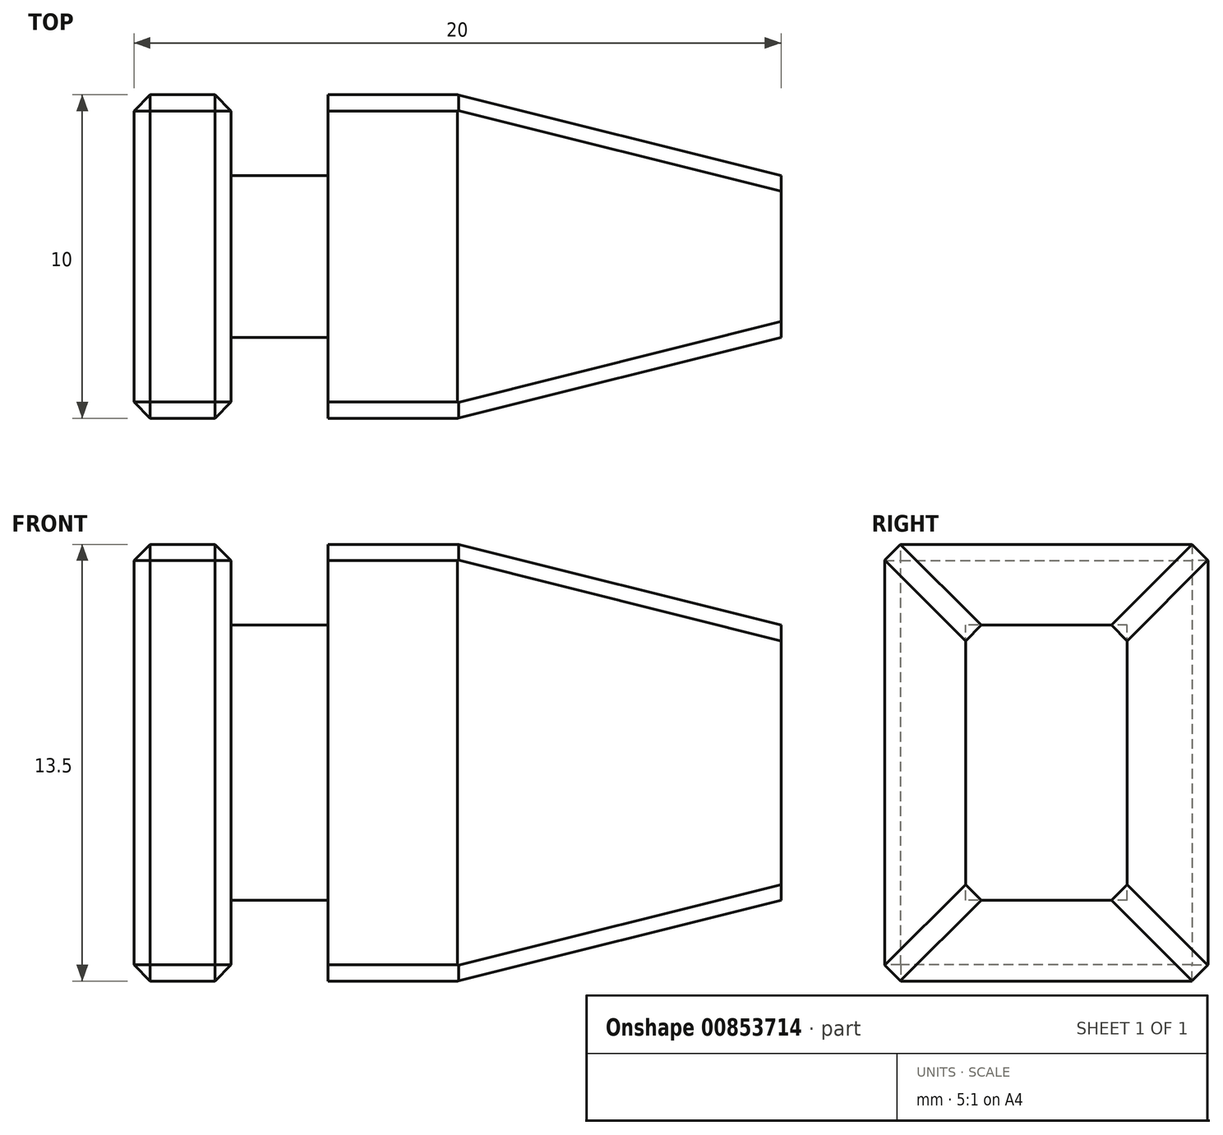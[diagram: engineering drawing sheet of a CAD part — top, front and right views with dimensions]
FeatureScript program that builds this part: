
annotation { "Feature Type Name" : "Feature", "Feature Type Description" : "" }
export const myFeature = defineFeature(function(context is Context, id is Id, definition is map)
    precondition{}
    {
        {
            var Q0;
            Q0=qCreatedBy(makeId("Front.planeOp"),FACE);
            var sketch = newSketch(context, id + "F0", { "sketchPlane" : qUnion([Q0])});
            skLineSegment(sketch, "E0.bottom", {"start": v(0, 0) * mm, "end": v(20, 0) * mm});
            skLineSegment(sketch, "E0.top", {"start": v(0, 13.5) * mm, "end": v(20, 13.5) * mm});
            skLineSegment(sketch, "E0.left", {"start": v(0, 0) * mm, "end": v(0, 13.5) * mm});
            skLineSegment(sketch, "E0.right", {"start": v(20, 0) * mm, "end": v(20, 13.5) * mm});
            skSolve(sketch);
        }
        {
            var Q0;
            Q0 = qSketchRegion(id + "F0", true);
            extrude(context, id + "F1", {"entities" : qUnion([Q0]), "depth" : 10 * mm, "offsetDistance" : 25 * mm});
        }
        {
            var Q0;
            Q0=makeQuery(id+"F1.opExtrude","CAP_FACE",FACE,{"disambiguationData":[OSD([sQuery(id+"F0.wireOp",EDGE,"E0.bottom"),sQuery(id+"F0.wireOp",EDGE,"E0.top"),sQuery(id+"F0.wireOp",EDGE,"E0.left"),sQuery(id+"F0.wireOp",EDGE,"E0.right")])],"isStart":false});
            var sketch = newSketch(context, id + "F2", { "sketchPlane" : qUnion([Q0])});
            skLineSegment(sketch, "E1.bottom", {"start": v(3, 13.5) * mm, "end": v(6, 13.5) * mm});
            skLineSegment(sketch, "E1.top", {"start": v(3, 11) * mm, "end": v(6, 11) * mm});
            skLineSegment(sketch, "E1.left", {"start": v(3, 13.5) * mm, "end": v(3, 11) * mm});
            skLineSegment(sketch, "E1.right", {"start": v(6, 13.5) * mm, "end": v(6, 11) * mm});
            skLineSegment(sketch, "E2", {"start": v(0, 6.75) * mm, "end": v(20, 6.75) * mm, "construction": true});
            skLineSegment(sketch, "E3.MirrorCS", {"start": v(6, 0) * mm, "end": v(6, 2.5) * mm});
            skLineSegment(sketch, "E4.MirrorCS", {"start": v(3, 2.5) * mm, "end": v(6, 2.5) * mm});
            skLineSegment(sketch, "E5.MirrorCS", {"start": v(3, 0) * mm, "end": v(6, 0) * mm});
            skLineSegment(sketch, "E6.MirrorCS", {"start": v(3, 0) * mm, "end": v(3, 2.5) * mm});
            skSolve(sketch);
        }
        {
            var Q0;
            Q0 = qSketchRegion(id + "F2", true);
            extrude(context, id + "F3", {"entities" : qUnion([Q0]), "operationType" : NewBodyOperationType.REMOVE, "oppositeDirection" : true, "depth" : 25 * mm, "offsetDistance" : 25 * mm});
        }
        {
            var Q0;
            {var subQ0=sQuery(id+"F0.wireOp",EDGE,"E0.right");var subQ2=sQuery(id+"F0.wireOp",EDGE,"E0.top");Q0=makeQuery(id+"F3.boolean.opBoolean","SPLIT",FACE,{"disambiguationData":[TD([makeQuery(id+"F1.opExtrude","SWEPT_FACE",FACE,{"disambiguationData":[OSD([subQ0])]})])],"derivedFrom":makeQuery(id+"F1.opExtrude","SWEPT_FACE",FACE,{"disambiguationData":[OSD([subQ2])]})});}
            var sketch = newSketch(context, id + "F4", { "sketchPlane" : qUnion([Q0])});
            skLineSegment(sketch, "E7", {"start": v(20, -5) * mm, "end": v(-8.74, -5) * mm, "construction": true});
            skLineSegment(sketch, "E8.bottom", {"start": v(6, 0) * mm, "end": v(3, 0) * mm});
            skLineSegment(sketch, "E8.top", {"start": v(6, -2.5) * mm, "end": v(3, -2.5) * mm});
            skLineSegment(sketch, "E8.left", {"start": v(6, 0) * mm, "end": v(6, -2.5) * mm});
            skLineSegment(sketch, "E8.right", {"start": v(3, 0) * mm, "end": v(3, -2.5) * mm});
            skLineSegment(sketch, "E9.MirrorCS", {"start": v(6, -10) * mm, "end": v(3, -10) * mm});
            skLineSegment(sketch, "E10.MirrorCS", {"start": v(3, -10) * mm, "end": v(3, -7.5) * mm});
            skLineSegment(sketch, "E11.MirrorCS", {"start": v(6, -10) * mm, "end": v(6, -7.5) * mm});
            skLineSegment(sketch, "E12.MirrorCS", {"start": v(6, -7.5) * mm, "end": v(3, -7.5) * mm});
            skSolve(sketch);
        }
        {
            var Q0;
            Q0=makeQuery(id+"F4.imprint","IMPRINT",FACE,{"disambiguationData":[TD([[makeQuery(id+"F4.imprint","IMPRINT",EDGE,{"derivedFrom":sQuery(id+"F4.wireOp",EDGE,"E8.bottom")}),1.0]])]});
            var Q1;
            Q1=makeQuery(id+"F4.imprint","IMPRINT",FACE,{"disambiguationData":[TD([[makeQuery(id+"F4.imprint","IMPRINT",EDGE,{"derivedFrom":sQuery(id+"F4.wireOp",EDGE,"E11.MirrorCS")}),-1.0]])]});
            extrude(context, id + "F5", {"entities" : qUnion([Q0, Q1]), "operationType" : NewBodyOperationType.REMOVE, "oppositeDirection" : true, "depth" : 25 * mm, "offsetDistance" : 25 * mm});
        }
        {
            var Q0;
            Q0=makeQuery(id+"F1.opExtrude","SWEPT_FACE",FACE,{"disambiguationData":[OSD([sQuery(id+"F0.wireOp",EDGE,"E0.right")])]});
            chamfer(context, id + "F6", {"entities" : qUnion([Q0]), "chamferType" : ChamferType.TWO_OFFSETS, "width1" : 2.5 * mm, "oppositeDirection" : false, "width2" : 10 * mm, "tangentPropagation" : true});
        }
        {
            var Q0;
            {var subQ0=sQuery(id+"F0.wireOp",EDGE,"E0.bottom");var subQ1=sQuery(id+"F0.wireOp",EDGE,"E0.right");Q0=makeQuery(id+"F3.boolean.opBoolean","SPLIT",EDGE,{"disambiguationData":[TD([makeQuery(id+"F1.opExtrude","SWEPT_FACE",FACE,{"disambiguationData":[OSD([subQ1])]})])],"derivedFrom":makeQuery(id+"F1.opExtrude","CAP_EDGE",EDGE,{"disambiguationData":[OSD([subQ0])],"isStart":false})});}
            var Q1;
            {var subQ0=sQuery(id+"F0.wireOp",EDGE,"E0.bottom");var subQ1=sQuery(id+"F0.wireOp",EDGE,"E0.left");Q1=makeQuery(id+"F3.boolean.opBoolean","SPLIT",EDGE,{"disambiguationData":[TD([makeQuery(id+"F1.opExtrude","SWEPT_FACE",FACE,{"disambiguationData":[OSD([subQ1])]})])],"derivedFrom":makeQuery(id+"F1.opExtrude","CAP_EDGE",EDGE,{"disambiguationData":[OSD([subQ0])],"isStart":false})});}
            var Q2;
            {var subQ0=sQuery(id+"F0.wireOp",EDGE,"E0.right");Q2=makeQuery(id+"F6.opChamfer","BLEND_EDGE",EDGE,{"blendedFrom":[makeQuery(id+"F1.opExtrude","SWEPT_EDGE",EDGE,{"disambiguationData":[OSD([sQuery(id+"F0.wireOp",EDGE,"E0.bottom"),subQ0])]}),makeQuery(id+"F1.opExtrude","CAP_EDGE",EDGE,{"disambiguationData":[OSD([subQ0])],"isStart":false})],"blendedInto":[]});}
            var Q3;
            {var subQ0=sQuery(id+"F0.wireOp",EDGE,"E0.bottom");var subQ1=sQuery(id+"F0.wireOp",EDGE,"E0.left");Q3=makeQuery(id+"F3.boolean.opBoolean","SPLIT",EDGE,{"disambiguationData":[TD([makeQuery(id+"F1.opExtrude","SWEPT_FACE",FACE,{"disambiguationData":[OSD([subQ1])]})])],"derivedFrom":makeQuery(id+"F1.opExtrude","CAP_EDGE",EDGE,{"disambiguationData":[OSD([subQ0])],"isStart":true})});}
            var Q4;
            {var subQ0=sQuery(id+"F0.wireOp",EDGE,"E0.bottom");var subQ1=sQuery(id+"F0.wireOp",EDGE,"E0.right");Q4=makeQuery(id+"F3.boolean.opBoolean","SPLIT",EDGE,{"disambiguationData":[TD([makeQuery(id+"F1.opExtrude","SWEPT_FACE",FACE,{"disambiguationData":[OSD([subQ1])]})])],"derivedFrom":makeQuery(id+"F1.opExtrude","CAP_EDGE",EDGE,{"disambiguationData":[OSD([subQ0])],"isStart":true})});}
            var Q5;
            {var subQ0=sQuery(id+"F0.wireOp",EDGE,"E0.right");Q5=makeQuery(id+"F6.opChamfer","BLEND_EDGE",EDGE,{"blendedFrom":[makeQuery(id+"F1.opExtrude","SWEPT_EDGE",EDGE,{"disambiguationData":[OSD([sQuery(id+"F0.wireOp",EDGE,"E0.bottom"),subQ0])]}),makeQuery(id+"F1.opExtrude","CAP_EDGE",EDGE,{"disambiguationData":[OSD([subQ0])],"isStart":true})],"blendedInto":[]});}
            var Q6;
            {var subQ0=sQuery(id+"F0.wireOp",EDGE,"E0.left");var subQ1=sQuery(id+"F0.wireOp",EDGE,"E0.top");var subQ2=sQuery(id+"F0.wireOp",EDGE,"E0.bottom");Q6=makeQuery(id+"F5.boolean.opBoolean","SPLIT",FACE,{"disambiguationData":[TD([makeQuery(id+"F1.opExtrude","SWEPT_FACE",FACE,{"disambiguationData":[OSD([subQ0])]})])],"derivedFrom":makeQuery(id+"F1.opExtrude","CAP_FACE",FACE,{"disambiguationData":[OSD([subQ2,subQ1,subQ0,sQuery(id+"F0.wireOp",EDGE,"E0.right")])],"isStart":true})});}
            var Q7;
            {var subQ1=sQuery(id+"F0.wireOp",EDGE,"E0.left");var subQ2=sQuery(id+"F0.wireOp",EDGE,"E0.top");Q7=makeQuery(id+"F3.boolean.opBoolean","SPLIT",FACE,{"disambiguationData":[TD([makeQuery(id+"F1.opExtrude","SWEPT_FACE",FACE,{"disambiguationData":[OSD([subQ1])]})])],"derivedFrom":makeQuery(id+"F1.opExtrude","SWEPT_FACE",FACE,{"disambiguationData":[OSD([subQ2])]})});}
            var Q8;
            {var subQ0=sQuery(id+"F0.wireOp",EDGE,"E0.right");var subQ1=sQuery(id+"F0.wireOp",EDGE,"E0.top");Q8=makeQuery(id+"F3.boolean.opBoolean","SPLIT",EDGE,{"disambiguationData":[TD([makeQuery(id+"F1.opExtrude","SWEPT_FACE",FACE,{"disambiguationData":[OSD([subQ0])]})])],"derivedFrom":makeQuery(id+"F1.opExtrude","CAP_EDGE",EDGE,{"disambiguationData":[OSD([subQ1])],"isStart":true})});}
            var Q9;
            {var subQ0=sQuery(id+"F0.wireOp",EDGE,"E0.right");Q9=makeQuery(id+"F6.opChamfer","BLEND_EDGE",EDGE,{"blendedFrom":[makeQuery(id+"F1.opExtrude","SWEPT_EDGE",EDGE,{"disambiguationData":[OSD([sQuery(id+"F0.wireOp",EDGE,"E0.top"),subQ0])]}),makeQuery(id+"F1.opExtrude","CAP_EDGE",EDGE,{"disambiguationData":[OSD([subQ0])],"isStart":true})],"blendedInto":[]});}
            var Q10;
            {var subQ0=sQuery(id+"F0.wireOp",EDGE,"E0.right");var subQ1=sQuery(id+"F0.wireOp",EDGE,"E0.top");Q10=makeQuery(id+"F3.boolean.opBoolean","SPLIT",EDGE,{"disambiguationData":[TD([makeQuery(id+"F1.opExtrude","SWEPT_FACE",FACE,{"disambiguationData":[OSD([subQ0])]})])],"derivedFrom":makeQuery(id+"F1.opExtrude","CAP_EDGE",EDGE,{"disambiguationData":[OSD([subQ1])],"isStart":false})});}
            var Q11;
            {var subQ0=sQuery(id+"F0.wireOp",EDGE,"E0.right");Q11=makeQuery(id+"F6.opChamfer","BLEND_EDGE",EDGE,{"blendedFrom":[makeQuery(id+"F1.opExtrude","SWEPT_EDGE",EDGE,{"disambiguationData":[OSD([sQuery(id+"F0.wireOp",EDGE,"E0.top"),subQ0])]}),makeQuery(id+"F1.opExtrude","CAP_EDGE",EDGE,{"disambiguationData":[OSD([subQ0])],"isStart":false})],"blendedInto":[]});}
            var Q12;
            {var subQ0=sQuery(id+"F0.wireOp",EDGE,"E0.left");var subQ1=sQuery(id+"F0.wireOp",EDGE,"E0.top");var subQ2=sQuery(id+"F0.wireOp",EDGE,"E0.bottom");Q12=makeQuery(id+"F5.boolean.opBoolean","SPLIT",FACE,{"disambiguationData":[TD([makeQuery(id+"F1.opExtrude","SWEPT_FACE",FACE,{"disambiguationData":[OSD([subQ0])]})])],"derivedFrom":makeQuery(id+"F1.opExtrude","CAP_FACE",FACE,{"disambiguationData":[OSD([subQ2,subQ1,subQ0,sQuery(id+"F0.wireOp",EDGE,"E0.right")])],"isStart":false})});}
            var Q13;
            {var subQ1=sQuery(id+"F0.wireOp",EDGE,"E0.left");var subQ3=sQuery(id+"F0.wireOp",EDGE,"E0.bottom");Q13=makeQuery(id+"F3.boolean.opBoolean","SPLIT",FACE,{"disambiguationData":[TD([makeQuery(id+"F1.opExtrude","SWEPT_FACE",FACE,{"disambiguationData":[OSD([subQ1])]})])],"derivedFrom":makeQuery(id+"F1.opExtrude","SWEPT_FACE",FACE,{"disambiguationData":[OSD([subQ3])]})});}
            chamfer(context, id + "F7", {"entities" : qUnion([Q0, Q1, Q2, Q3, Q4, Q5, Q6, Q7, Q8, Q9, Q10, Q11, Q12, Q13]), "width" : .5 * mm, "tangentPropagation" : true});
        }
    });
